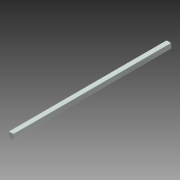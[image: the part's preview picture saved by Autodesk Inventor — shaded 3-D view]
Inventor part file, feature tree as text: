
AUTODESK INVENTOR PART (.ipt)
format: ipt  version: 2013 (Build 170138000, 138)  size: 150,016 bytes
history: native  units: in
note: dims shown in document units (in); Inventor stores cm internally (conversion verified against a paired STEP export)
features: sketch x2, plane x2, extrude x1, revolve x1, mirror x1, other x1
ambient origin geometry x8: Origin, YZ Plane, XZ Plane, XY Plane, X Axis, Y Axis, Z Axis, Center Point
bodies: Solid1 (feature_tree)
feature tree (8):
  sketch  "Sketch1"  dims[d0=4.0in d1=0.0in d2=90.0deg]
  extrude  "Extrusion1"  TaperAngle=90.0deg  [1 undecoded]
  plane  "Work Plane1"
  revolve  "Revolution1"  [1 undecoded]
  plane  "Work Plane2"
  mirror  "Mirror1"
  other  "Work Axis1"
  sketch  "Sketch2"  dims[d3=90.0deg]
note: 2 required parameter values undecoded (feature->parameter linkage not recoverable at this tier; creation-order binding heuristic only, values carry confidence <= 0.55)
